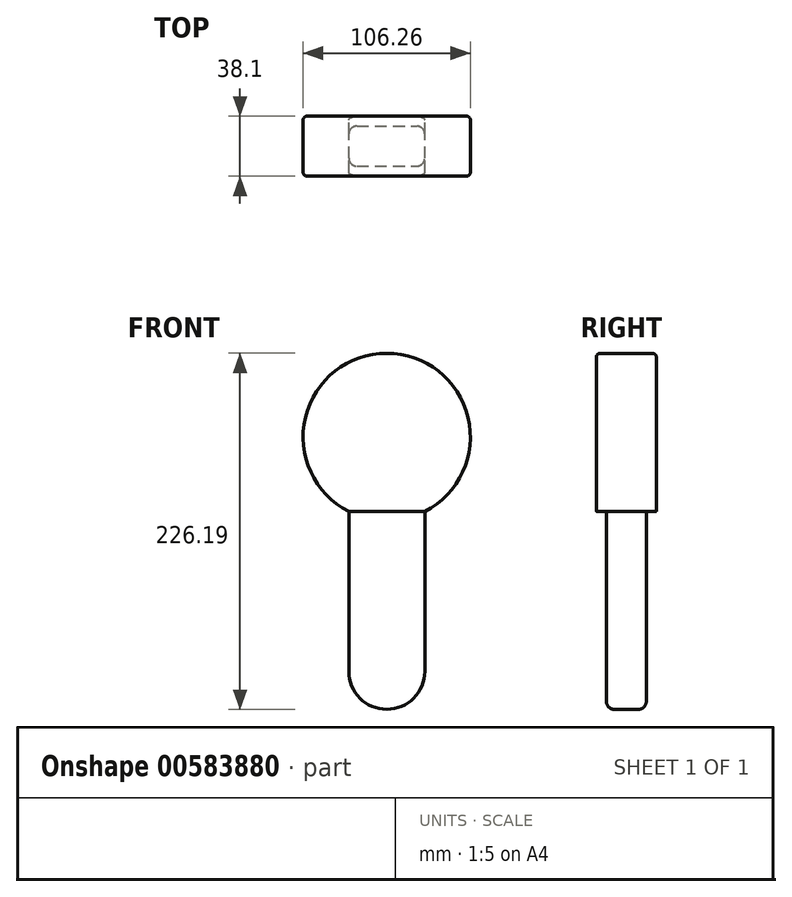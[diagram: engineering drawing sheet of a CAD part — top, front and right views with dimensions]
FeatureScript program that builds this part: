
annotation { "Feature Type Name" : "Feature", "Feature Type Description" : "" }
export const myFeature = defineFeature(function(context is Context, id is Id, definition is map)
    precondition{}
    {
        {
            var Q0;
            Q0=qCreatedBy(makeId("Front.planeOp"),FACE);
            var sketch = newSketch(context, id + "F0", { "sketchPlane" : qUnion([Q0])});
            skArc(sketch, "E0", {"start": v(24.14, -47.33) * mm, "mid": v(-0.01, 53.13) * mm, "end": v(-24.12, -47.34) * mm});
            skLineSegment(sketch, "E1", {"start": v(-24.12, -45.72) * mm, "end": v(-24.12, -148.93) * mm});
            skLineSegment(sketch, "E2", {"start": v(24.14, -148.93) * mm, "end": v(24.14, -47.33) * mm});
            skPoint(sketch, "E3", {"position": v(-24.12, -45.72) * mm});
            skPoint(sketch, "E4", {"position": v(27.06, -45.72) * mm});
            skPoint(sketch, "E5.orphan", {"position": v(24.14, 0) * mm});
            skPoint(sketch, "E6.orphan", {"position": v(-24.12, 0) * mm});
            skArc(sketch, "E7", {"start": v(-24.12, -148.93) * mm, "mid": v(0.01, -173.06) * mm, "end": v(24.14, -148.93) * mm});
            skLineSegment(sketch, "E8", {"start": v(-24.12, -47.34) * mm, "end": v(24.14, -47.33) * mm});
            skPoint(sketch, "E9", {"position": v(0, 53.13) * mm});
            skPoint(sketch, "E9.positionSnap0", {"position": v(-0.01, 53.13) * mm});
            skPoint(sketch, "E10", {"position": v(0, -173.06) * mm});
            skPoint(sketch, "E10.positionSnap0", {"position": v(0.01, -173.06) * mm});
            skSolve(sketch);
        }
        {
            var Q0;
            Q0=makeQuery(id+"F0.imprint","IMPRINT",FACE,{"disambiguationData":[TD([[makeQuery(id+"F0.imprint","IMPRINT",EDGE,{"derivedFrom":sQuery(id+"F0.wireOp",EDGE,"E0")}),1.0]])]});
            extrude(context, id + "F1", {"entities" : qUnion([Q0]), "endBound" : BoundingType.SYMMETRIC, "depth" : 38.1 * mm, "offsetDistance" : 25.4 * mm});
        }
        {
            var Q0;
            Q0=makeQuery(id+"F1.opExtrude","CAP_EDGE",EDGE,{"disambiguationData":[OSD([sQuery(id+"F0.wireOp",EDGE,"E0")])],"isStart":false});
            var Q1;
            Q1=makeQuery(id+"F1.opExtrude","CAP_EDGE",EDGE,{"disambiguationData":[OSD([sQuery(id+"F0.wireOp",EDGE,"E0")])],"isStart":true});
            fillet(context, id + "F2", {"entities" : qUnion([Q0, Q1]), "radius" : 2.54 * mm, "tangentPropagation" : true, "allowEdgeOverflow" : false});
        }
        {
            var Q0;
            Q0=makeQuery(id+"F0.imprint","IMPRINT",FACE,{"disambiguationData":[TD([[makeQuery(id+"F0.imprint","IMPRINT",EDGE,{"derivedFrom":sQuery(id+"F0.wireOp",EDGE,"E2")}),1.0]])]});
            extrude(context, id + "F3", {"entities" : qUnion([Q0]), "operationType" : NewBodyOperationType.ADD, "endBound" : BoundingType.SYMMETRIC, "depth" : 25.4 * mm, "offsetDistance" : 25.4 * mm});
        }
        {
            var Q0;
            Q0=makeQuery(id+"F3.opExtrude","CAP_EDGE",EDGE,{"disambiguationData":[OSD([sQuery(id+"F0.wireOp",EDGE,"E1")])],"isStart":true});
            var Q1;
            Q1=makeQuery(id+"F3.opExtrude","CAP_EDGE",EDGE,{"disambiguationData":[OSD([sQuery(id+"F0.wireOp",EDGE,"E1")])],"isStart":false});
            var Q2;
            Q2=makeQuery(id+"F3.opExtrude","CAP_EDGE",EDGE,{"disambiguationData":[OSD([sQuery(id+"F0.wireOp",EDGE,"E2")])],"isStart":false});
            var Q3;
            Q3=makeQuery(id+"F3.opExtrude","CAP_EDGE",EDGE,{"disambiguationData":[OSD([sQuery(id+"F0.wireOp",EDGE,"E2")])],"isStart":true});
            fillet(context, id + "F4", {"entities" : qUnion([Q0, Q1, Q2, Q3]), "radius" : 5.08 * mm, "tangentPropagation" : true, "allowEdgeOverflow" : false});
        }
    });
